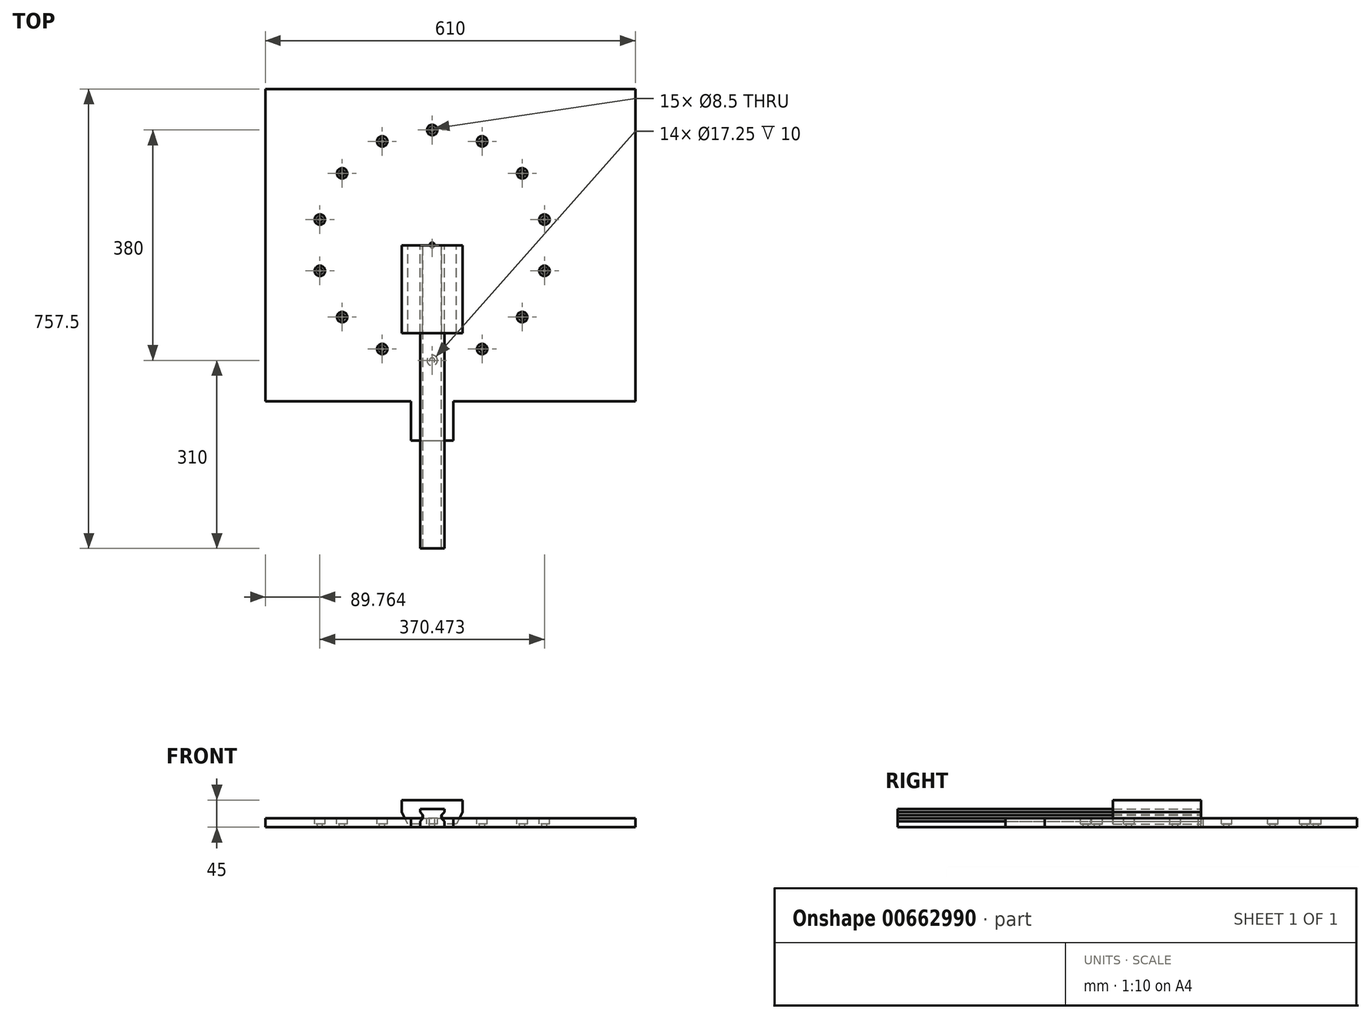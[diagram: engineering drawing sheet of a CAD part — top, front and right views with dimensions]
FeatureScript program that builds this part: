
annotation { "Feature Type Name" : "Feature", "Feature Type Description" : "" }
export const myFeature = defineFeature(function(context is Context, id is Id, definition is map)
    precondition{}
    {
        {
            var Q0;
            Q0=qCreatedBy(makeId("Top.planeOp"),FACE);
            var sketch = newSketch(context, id + "F0", { "sketchPlane" : qUnion([Q0])});
            skLineSegment(sketch, "E0.bottom", {"start": v(335, -257.5) * mm, "end": v(-275, -257.5) * mm});
            skLineSegment(sketch, "E0.top", {"start": v(335, 257.5) * mm, "end": v(-275, 257.5) * mm});
            skLineSegment(sketch, "E0.left", {"start": v(335, -257.5) * mm, "end": v(335, 257.5) * mm});
            skLineSegment(sketch, "E0.right", {"start": v(-275, -257.5) * mm, "end": v(-275, 257.5) * mm});
            skPoint(sketch, "E0.middle", {"position": v(30, 0) * mm});
            skLineSegment(sketch, "E1", {"start": v(0, 0) * mm, "end": v(0, -257.5) * mm, "construction": true});
            skLineSegment(sketch, "E2", {"start": v(0, -257.5) * mm, "end": v(0, -290) * mm, "construction": true});
            skLineSegment(sketch, "E3.bottom", {"start": v(-35, -257.5) * mm, "end": v(35, -257.5) * mm});
            skLineSegment(sketch, "E3.top", {"start": v(-35, -322.5) * mm, "end": v(35, -322.5) * mm});
            skLineSegment(sketch, "E3.left", {"start": v(-35, -257.5) * mm, "end": v(-35, -322.5) * mm});
            skLineSegment(sketch, "E3.right", {"start": v(35, -257.5) * mm, "end": v(35, -322.5) * mm});
            skPoint(sketch, "E3.middle", {"position": v(0, -290) * mm});
            skSolve(sketch);
        }
        {
            var Q0;
            Q0=makeQuery(id+"F0.imprint","IMPRINT",FACE,{"disambiguationData":[TD([[makeQuery(id+"F0.imprint","IMPRINT",EDGE,{"derivedFrom":sQuery(id+"F0.wireOp",EDGE,"E0.bottom")}),-1.0]])]});
            var Q1;
            Q1=makeQuery(id+"F0.imprint","IMPRINT",FACE,{"disambiguationData":[TD([[makeQuery(id+"F0.imprint","IMPRINT",EDGE,{"derivedFrom":sQuery(id+"F0.wireOp",EDGE,"E3.top")}),1.0]])]});
            extrude(context, id + "F1", {"entities" : qUnion([Q0, Q1]), "depth" : 15 * mm, "offsetDistance" : 25 * mm});
        }
        {
            var Q0;
            Q0=makeQuery(id+"F1.opExtrude","CAP_FACE",FACE,{"disambiguationData":[OSD([sQuery(id+"F0.wireOp",EDGE,"E0.bottom"),sQuery(id+"F0.wireOp",EDGE,"E0.top"),sQuery(id+"F0.wireOp",EDGE,"E0.left"),sQuery(id+"F0.wireOp",EDGE,"E0.right")])],"isStart":false});
            var sketch = newSketch(context, id + "F2", { "sketchPlane" : qUnion([Q0])});
            skCircle(sketch, "E4", {"center": v(0, 0) * mm, "radius": 190 * mm, "construction": true});
            skPoint(sketch, "E5", {"position": v(0, 190) * mm});
            skLineSegment(sketch, "E6", {"start": v(0, 190) * mm, "end": v(0, 0) * mm, "construction": true});
            skPoint(sketch, "E7.1.0", {"position": v(-82.44, 171.18) * mm});
            skPoint(sketch, "E7.2.0", {"position": v(-148.55, 118.46) * mm});
            skPoint(sketch, "E7.3.0", {"position": v(-185.24, 42.28) * mm});
            skPoint(sketch, "E7.4.0", {"position": v(-185.24, -42.28) * mm});
            skPoint(sketch, "E7.5.0", {"position": v(-148.55, -118.46) * mm});
            skPoint(sketch, "E7.6.0", {"position": v(-82.44, -171.18) * mm});
            skPoint(sketch, "E7.7.0", {"position": v(0, -190) * mm});
            skPoint(sketch, "E7.8.0", {"position": v(82.44, -171.18) * mm});
            skPoint(sketch, "E7.9.0", {"position": v(148.55, -118.46) * mm});
            skPoint(sketch, "E7.10.0", {"position": v(185.24, -42.28) * mm});
            skPoint(sketch, "E7.11.0", {"position": v(185.24, 42.28) * mm});
            skPoint(sketch, "E7.12.0", {"position": v(148.55, 118.46) * mm});
            skPoint(sketch, "E7.13.0", {"position": v(82.44, 171.18) * mm});
            skSolve(sketch);
        }
        {
            var Q0;
            Q0=sQuery(id+"F2.wireOp",VERTEX,"E5");
            var Q1;
            Q1=sQuery(id+"F2.wireOp",VERTEX,"E7.13.0");
            var Q2;
            Q2=sQuery(id+"F2.wireOp",VERTEX,"E7.12.0");
            var Q3;
            Q3=sQuery(id+"F2.wireOp",VERTEX,"E7.11.0");
            var Q4;
            Q4=sQuery(id+"F2.wireOp",VERTEX,"E7.10.0");
            var Q5;
            Q5=sQuery(id+"F2.wireOp",VERTEX,"E7.9.0");
            var Q6;
            Q6=sQuery(id+"F2.wireOp",VERTEX,"E7.8.0");
            var Q7;
            Q7=sQuery(id+"F2.wireOp",VERTEX,"E7.7.0");
            var Q8;
            Q8=sQuery(id+"F2.wireOp",VERTEX,"E7.6.0");
            var Q9;
            Q9=sQuery(id+"F2.wireOp",VERTEX,"E7.5.0");
            var Q10;
            Q10=sQuery(id+"F2.wireOp",VERTEX,"E7.4.0");
            var Q11;
            Q11=sQuery(id+"F2.wireOp",VERTEX,"E7.3.0");
            var Q12;
            Q12=sQuery(id+"F2.wireOp",VERTEX,"E7.2.0");
            var Q13;
            Q13=sQuery(id+"F2.wireOp",VERTEX,"E7.1.0");
            var Q14;
            Q14=makeQuery(id+"F1.opExtrude","SWEPT_BODY",BODY,{"disambiguationData":[OSD([sQuery(id+"F0.wireOp",EDGE,"E0.bottom"),sQuery(id+"F0.wireOp",EDGE,"E0.top"),sQuery(id+"F0.wireOp",EDGE,"E0.left"),sQuery(id+"F0.wireOp",EDGE,"E0.right")])]});
            hole(context, id + "F3", {"style" : HoleStyle.C_BORE, "endStyle" : HoleEndStyle.THROUGH, "standardTappedOrClearance" : lookupTablePath({ "standard" : "ISO", "engagement" : "75%", "pitch" : "1.5 mm", "size" : "M10", "type" : "Tapped" }), "standardBlindInLast" : lookupTablePath({ "fit" : "Normal", "standard" : "ISO", "engagement" : "75%", "pitch" : "1.5 mm", "size" : "M10", "type" : "Clearance & tapped" }), "holeDiameter" : 8.5 * mm, "cBoreDiameter" : 17.25 * mm, "cBoreDepth" : 10 * mm, "majorDiameter" : 10 * mm, "showTappedDepth" : true, "isTappedThrough" : true, "tappedDepth" : 12 * mm, "tapClearance" : 3, "locations" : qUnion([Q0, Q1, Q2, Q3, Q4, Q5, Q6, Q7, Q8, Q9, Q10, Q11, Q12, Q13]), "scope" : qUnion([Q14])});
        }
        {
            var Q0;
            Q0=qCreatedBy(makeId("Front.planeOp"),FACE);
            var sketch = newSketch(context, id + "F4", { "sketchPlane" : qUnion([Q0])});
            skLineSegment(sketch, "E8", {"start": v(0, 0) * mm, "end": v(-20, 0) * mm});
            skLineSegment(sketch, "E9", {"start": v(-20, 0) * mm, "end": v(-20, 10) * mm});
            skLineSegment(sketch, "E10", {"start": v(-20, 10) * mm, "end": v(-15, 15) * mm});
            skLineSegment(sketch, "E11", {"start": v(-15, 15) * mm, "end": v(-15, 20) * mm});
            skLineSegment(sketch, "E12", {"start": v(-15, 20) * mm, "end": v(-20, 25) * mm});
            skLineSegment(sketch, "E13", {"start": v(-20, 25) * mm, "end": v(-20, 30) * mm});
            skLineSegment(sketch, "E14", {"start": v(-20, 30) * mm, "end": v(0, 30) * mm});
            skLineSegment(sketch, "E15", {"start": v(0, 30) * mm, "end": v(20, 30) * mm});
            skLineSegment(sketch, "E16", {"start": v(20, 30) * mm, "end": v(20, 25) * mm});
            skLineSegment(sketch, "E17", {"start": v(20, 25) * mm, "end": v(15, 20) * mm});
            skLineSegment(sketch, "E18", {"start": v(15, 20) * mm, "end": v(15, 15) * mm});
            skLineSegment(sketch, "E19", {"start": v(15, 15) * mm, "end": v(20, 10) * mm});
            skLineSegment(sketch, "E20", {"start": v(20, 10) * mm, "end": v(20, 0) * mm});
            skLineSegment(sketch, "E21", {"start": v(20, 0) * mm, "end": v(0, 0) * mm});
            skLineSegment(sketch, "E22", {"start": v(-50, 45) * mm, "end": v(0, 45) * mm});
            skLineSegment(sketch, "E23", {"start": v(50, 45) * mm, "end": v(50, 25) * mm});
            skLineSegment(sketch, "E24", {"start": v(50, 25) * mm, "end": v(40, 5) * mm});
            skLineSegment(sketch, "E25", {"start": v(40, 5) * mm, "end": v(20, 5) * mm});
            skLineSegment(sketch, "E26", {"start": v(-20, 5) * mm, "end": v(-40, 5) * mm});
            skLineSegment(sketch, "E27", {"start": v(-40, 5) * mm, "end": v(-50, 25) * mm});
            skLineSegment(sketch, "E28", {"start": v(-50, 25) * mm, "end": v(-50, 45) * mm});
            skLineSegment(sketch, "E29", {"start": v(0, 45) * mm, "end": v(50, 45) * mm});
            skLineSegment(sketch, "E30", {"start": v(-16, 14) * mm, "end": v(-16, 21) * mm});
            skLineSegment(sketch, "E31", {"start": v(16, 14) * mm, "end": v(16, 21) * mm});
            skSolve(sketch);
        }
        {
            var Q0;
            Q0=makeQuery(id+"F4.imprint","IMPRINT",FACE,{"disambiguationData":[TD([[makeQuery(id+"F4.imprint","IMPRINT",EDGE,{"derivedFrom":sQuery(id+"F4.wireOp",EDGE,"E8")}),-1.0]])]});
            extrude(context, id + "F5", {"entities" : qUnion([Q0]), "depth" : 500 * mm, "offsetDistance" : 25 * mm});
        }
        {
            var Q0;
            {var subQ12=sQuery(id+"F4.wireOp",EDGE,"E13");Q0=makeQuery(id+"F4.imprint","IMPRINT",FACE,{"disambiguationData":[TD([[makeQuery(id+"F4.imprint","IMPRINT",EDGE,{"derivedFrom":subQ12}),1.0]])]});}
            extrude(context, id + "F6", {"entities" : qUnion([Q0]), "depth" : 145 * mm, "offsetDistance" : 25 * mm});
        }
        {
            var Q0;
            Q0=makeQuery(id+"F1.opExtrude","CAP_FACE",FACE,{"disambiguationData":[OSD([sQuery(id+"F0.wireOp",EDGE,"E0.bottom"),sQuery(id+"F0.wireOp",EDGE,"E0.top"),sQuery(id+"F0.wireOp",EDGE,"E0.left"),sQuery(id+"F0.wireOp",EDGE,"E0.right"),sQuery(id+"F0.wireOp",EDGE,"E3.top"),sQuery(id+"F0.wireOp",EDGE,"E3.left"),sQuery(id+"F0.wireOp",EDGE,"E3.right")])],"isStart":false});
            var sketch = newSketch(context, id + "F7", { "sketchPlane" : qUnion([Q0])});
            skPoint(sketch, "E32", {"position": v(0, 0) * mm});
            skSolve(sketch);
        }
        {
            var Q0;
            Q0=sQuery(id+"F7.wireOp",VERTEX,"E32");
            var Q1;
            Q1=makeQuery(id+"F1.opExtrude","SWEPT_BODY",BODY,{"disambiguationData":[OSD([sQuery(id+"F0.wireOp",EDGE,"E0.bottom"),sQuery(id+"F0.wireOp",EDGE,"E0.top"),sQuery(id+"F0.wireOp",EDGE,"E0.left"),sQuery(id+"F0.wireOp",EDGE,"E0.right"),sQuery(id+"F0.wireOp",EDGE,"E3.top"),sQuery(id+"F0.wireOp",EDGE,"E3.left"),sQuery(id+"F0.wireOp",EDGE,"E3.right")])]});
            hole(context, id + "F8", {"style" : HoleStyle.SIMPLE, "endStyle" : HoleEndStyle.THROUGH, "standardTappedOrClearance" : lookupTablePath({ "standard" : "ISO", "engagement" : "75%", "pitch" : "1.5 mm", "size" : "M10", "type" : "Tapped" }), "standardBlindInLast" : lookupTablePath({ "fit" : "Normal", "standard" : "ISO", "engagement" : "75%", "pitch" : "1.5 mm", "size" : "M10", "type" : "Clearance & tapped" }), "holeDiameter" : 8.5 * mm, "majorDiameter" : 10 * mm, "showTappedDepth" : true, "isTappedThrough" : true, "tappedDepth" : 12 * mm, "tapClearance" : 3, "locations" : qUnion([Q0]), "scope" : qUnion([Q1])});
        }
    });
